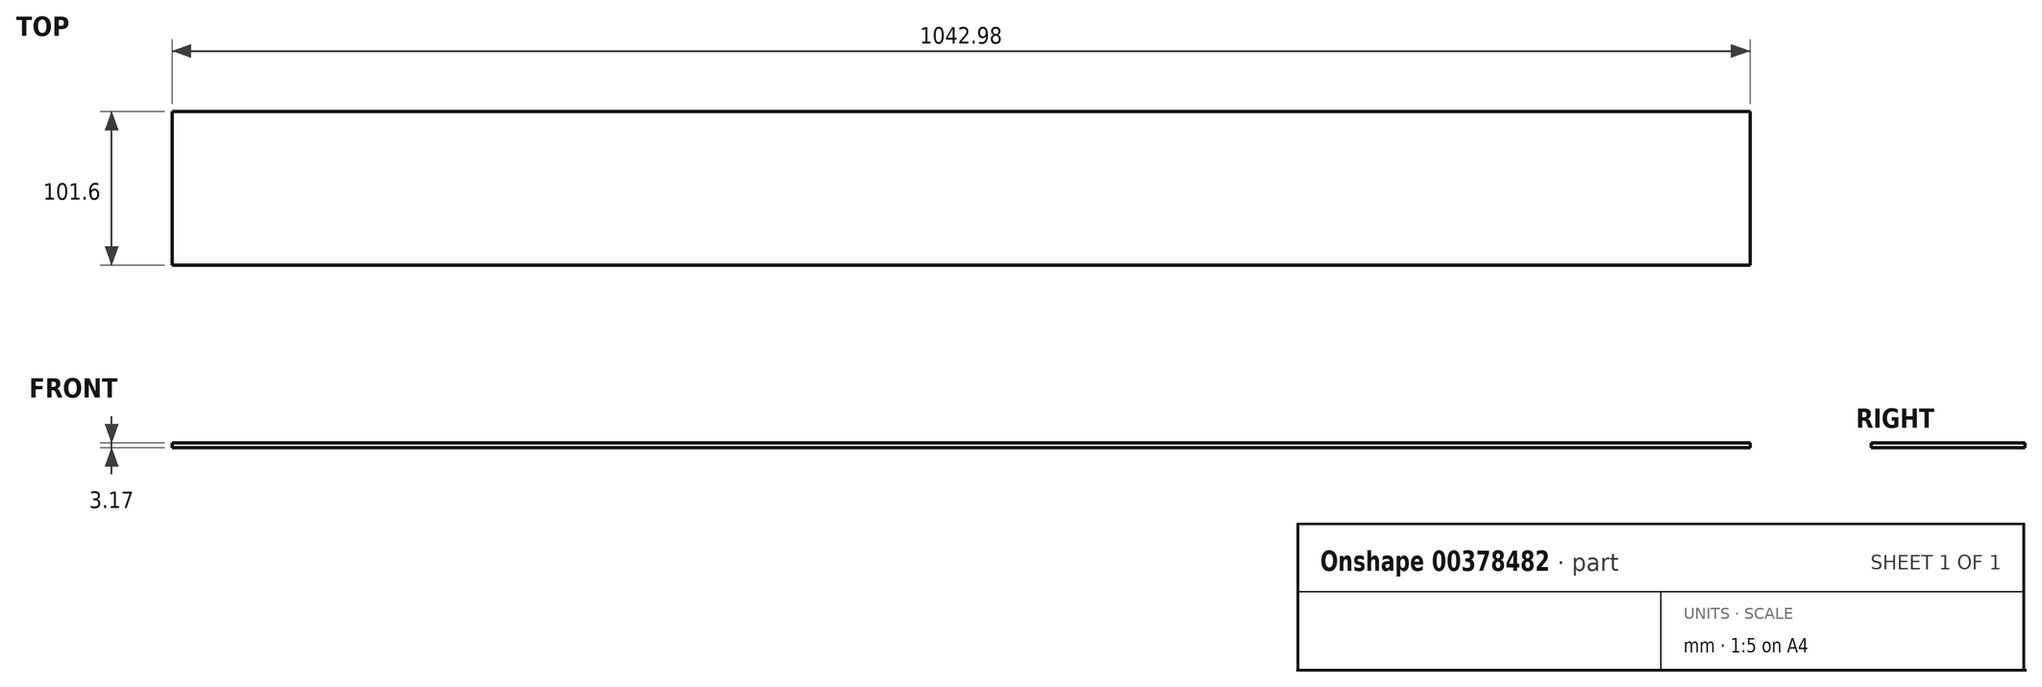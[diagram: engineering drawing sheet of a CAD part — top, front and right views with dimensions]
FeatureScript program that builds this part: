
annotation { "Feature Type Name" : "Feature", "Feature Type Description" : "" }
export const myFeature = defineFeature(function(context is Context, id is Id, definition is map)
    precondition{}
    {
        {
            var Q0;
            Q0=qCreatedBy(makeId("Top.planeOp"),FACE);
            var sketch = newSketch(context, id + "F0", { "sketchPlane" : qUnion([Q0])});
            skLineSegment(sketch, "E0.bottom", {"start": v(521.5, 50.8) * mm, "end": v(-521.5, 50.8) * mm});
            skLineSegment(sketch, "E0.top", {"start": v(521.5, -50.8) * mm, "end": v(-521.5, -50.8) * mm});
            skLineSegment(sketch, "E0.left", {"start": v(521.5, 50.8) * mm, "end": v(521.5, -50.8) * mm});
            skLineSegment(sketch, "E0.right", {"start": v(-521.5, 50.8) * mm, "end": v(-521.5, -50.8) * mm});
            skPoint(sketch, "E0.middle", {"position": v(0, 0) * mm});
            skSolve(sketch);
        }
        {
            var Q0;
            Q0 = qSketchRegion(id + "F0", true);
            extrude(context, id + "F1", {"entities" : qUnion([Q0]), "depth" : 3.17 * mm});
        }
    });
